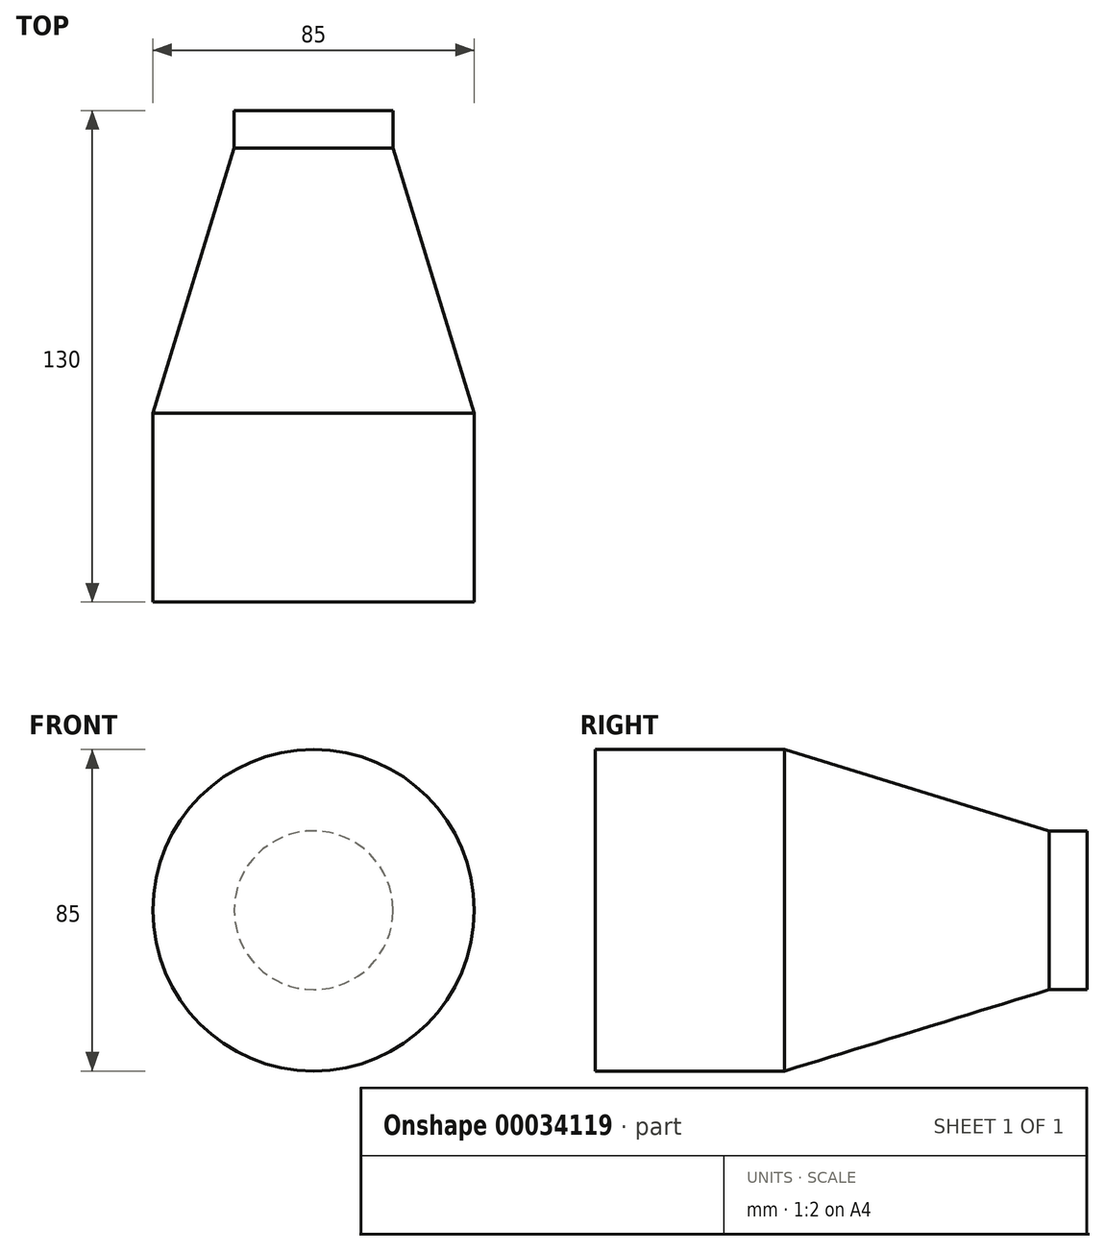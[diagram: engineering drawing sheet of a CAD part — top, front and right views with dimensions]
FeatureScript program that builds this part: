
annotation { "Feature Type Name" : "Feature", "Feature Type Description" : "" }
export const myFeature = defineFeature(function(context is Context, id is Id, definition is map)
    precondition{}
    {
        {
            var Q0;
            Q0=qCreatedBy(makeId("Front.planeOp"),FACE);
            var sketch = newSketch(context, id + "F0", { "sketchPlane" : qUnion([Q0])});
            skCircle(sketch, "E0", {"center": v(0, 0) * mm, "radius": 42.5 * mm});
            skSolve(sketch);
        }
        {
            var Q0;
            Q0=qCreatedBy(makeId("Front.planeOp"),FACE);
            cPlane(context, id + "F1", {"entities" : qUnion([Q0]), "cplaneType" : CPlaneType.OFFSET, "offset" : 120 * mm, "oppositeDirection" : true, "width" : 150 * mm, "height" : 150 * mm});
        }
        {
            var Q0;
            Q0=qCreatedBy(id+"F1.planeOp",FACE);
            var sketch = newSketch(context, id + "F2", { "sketchPlane" : qUnion([Q0])});
            skCircle(sketch, "E1", {"center": v(0, 0) * mm, "radius": 21 * mm});
            skSolve(sketch);
        }
        {
            var Q0;
            Q0 = qSketchRegion(id + "F2", true);
            extrude(context, id + "F3", {"entities" : qUnion([Q0]), "oppositeDirection" : true, "depth" : 10 * mm});
        }
        {
            var Q0;
            Q0=makeQuery(id+"F0.imprint","IMPRINT",FACE,{"disambiguationData":[TD([[makeQuery(id+"F0.imprint","IMPRINT",EDGE,{"derivedFrom":sQuery(id+"F0.wireOp",EDGE,"E0")}),1.0]])]});
            extrude(context, id + "F4", {"entities" : qUnion([Q0]), "oppositeDirection" : true, "depth" : 50 * mm});
        }
        {
            var Q0;
            Q0=makeQuery(id+"F4.opExtrude","CAP_FACE",FACE,{"disambiguationData":[OSD([sQuery(id+"F0.wireOp",EDGE,"E0")])],"isStart":false});
            var Q1;
            Q1=makeQuery(id+"F3.opExtrude","CAP_FACE",FACE,{"disambiguationData":[OSD([sQuery(id+"F2.wireOp",EDGE,"E1")])],"isStart":true});
            loft(context, id + "F5", {"sheetProfilesArray" : [{ "sheetProfileEntities" : qUnion([Q0]) }, { "sheetProfileEntities" : qUnion([Q1]) }]});
        }
        {
            var Q0;
            Q0=makeQuery(id+"F4.opExtrude","SWEPT_BODY",BODY,{"disambiguationData":[OSD([sQuery(id+"F0.wireOp",EDGE,"E0")])]});
            deleteBodies(context, id + "F6", {"entities" : qUnion([Q0])});
        }
        {
            var Q0;
            Q0=makeQuery(id+"F5.opLoft","CAP_FACE",FACE,{"disambiguationData":[OSD([sQuery(id+"F0.wireOp",EDGE,"E0")])],"isStart":true});
            extrude(context, id + "F7", {"entities" : qUnion([Q0]), "operationType" : NewBodyOperationType.ADD, "depth" : 50 * mm});
        }
    });
